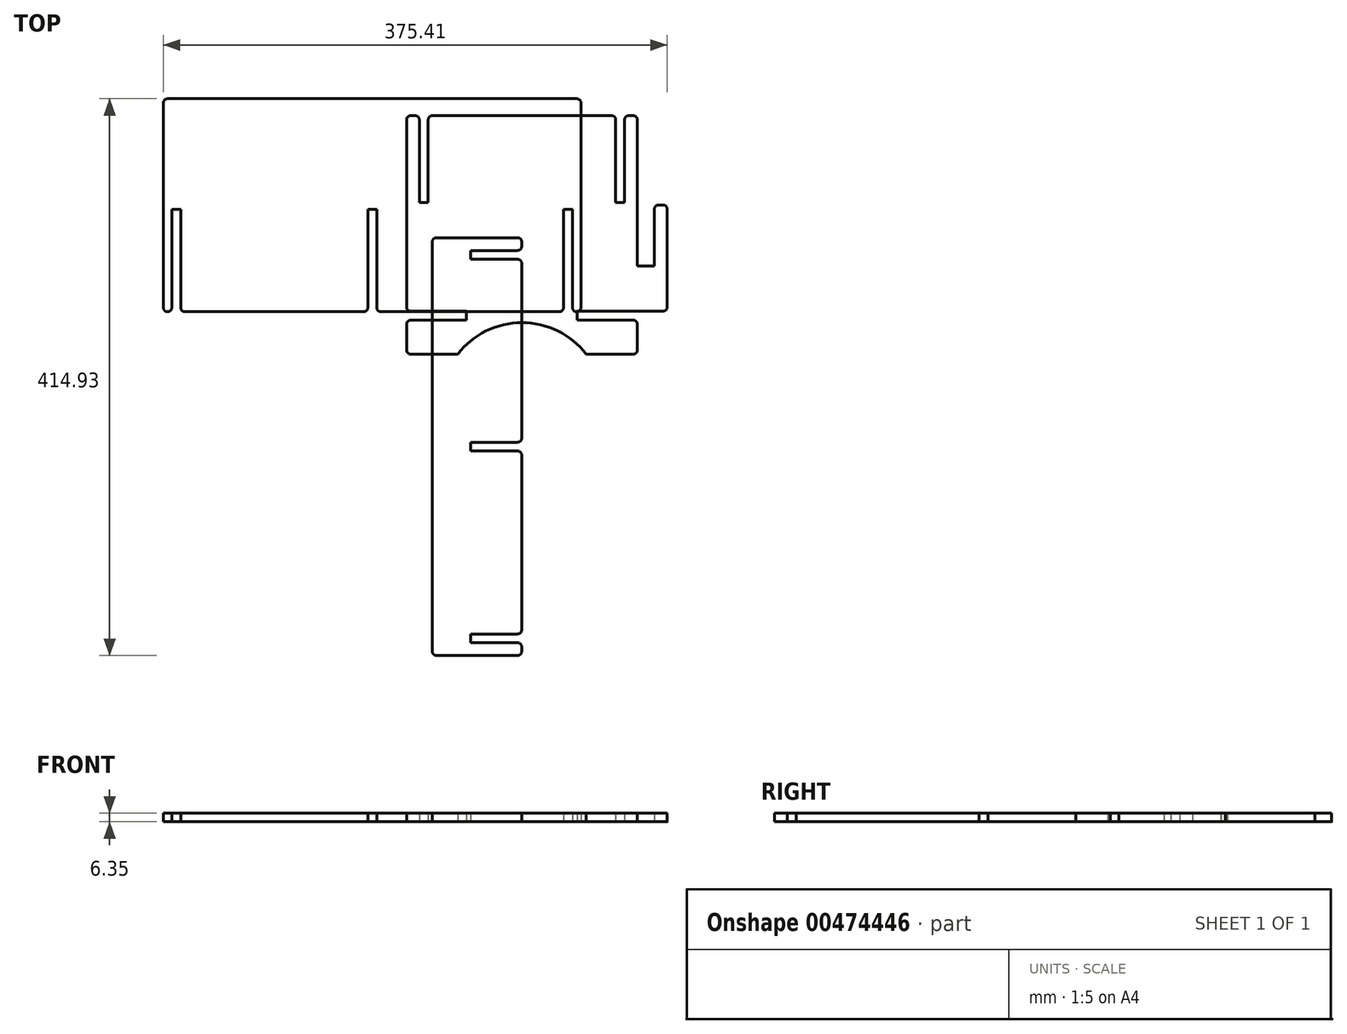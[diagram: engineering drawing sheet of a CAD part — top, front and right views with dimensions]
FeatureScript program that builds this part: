
annotation { "Feature Type Name" : "Feature", "Feature Type Description" : "" }
export const myFeature = defineFeature(function(context is Context, id is Id, definition is map)
    precondition{}
    {
        {
            var Q0;
            Q0=qCreatedBy(makeId("Top.planeOp"),FACE);
            var sketch = newSketch(context, id + "F0", { "sketchPlane" : qUnion([Q0])});
            skLineSegment(sketch, "E0", {"start": v(0, 9.78) * mm, "end": v(0, 149.22) * mm});
            skLineSegment(sketch, "E1", {"start": v(3.17, 152.4) * mm, "end": v(6.35, 152.4) * mm});
            skLineSegment(sketch, "E2", {"start": v(3.17, 0) * mm, "end": v(44.45, 0) * mm});
            skLineSegment(sketch, "E3", {"start": v(171.96, 149.22) * mm, "end": v(171.96, 40.3) * mm});
            skLineSegment(sketch, "E4", {"start": v(168.78, -25.4) * mm, "end": v(133.86, -25.4) * mm});
            skLineSegment(sketch, "E5", {"start": v(0, -3.18) * mm, "end": v(0, -22.22) * mm});
            skLineSegment(sketch, "E6", {"start": v(3.18, -25.4) * mm, "end": v(38.1, -25.4) * mm});
            skLineSegment(sketch, "E7", {"start": v(171.96, -22.23) * mm, "end": v(171.96, -3.18) * mm});
            skLineSegment(sketch, "E8", {"start": v(3.17, 6.6) * mm, "end": v(44.45, 6.6) * mm});
            skLineSegment(sketch, "E9", {"start": v(44.45, 6.6) * mm, "end": v(44.45, 0) * mm});
            skLineSegment(sketch, "E10", {"start": v(171.96, 6.6) * mm, "end": v(127, 6.6) * mm});
            skLineSegment(sketch, "E11", {"start": v(127, 6.6) * mm, "end": v(127, 0) * mm});
            skLineSegment(sketch, "E12", {"start": v(9.53, 149.22) * mm, "end": v(9.53, 87.56) * mm});
            skLineSegment(sketch, "E13", {"start": v(9.53, 87.56) * mm, "end": v(16.13, 87.56) * mm});
            skLineSegment(sketch, "E14", {"start": v(16.13, 87.56) * mm, "end": v(16.13, 149.22) * mm});
            skLineSegment(sketch, "E15.trimOffspring", {"start": v(19.3, 152.4) * mm, "end": v(152.65, 152.4) * mm});
            skLineSegment(sketch, "E16", {"start": v(162.43, 149.22) * mm, "end": v(162.43, 87.56) * mm});
            skLineSegment(sketch, "E17", {"start": v(162.43, 87.56) * mm, "end": v(155.83, 87.56) * mm});
            skLineSegment(sketch, "E18", {"start": v(155.83, 87.56) * mm, "end": v(155.83, 149.22) * mm});
            skLineSegment(sketch, "E19.trimOffspring", {"start": v(165.6, 152.4) * mm, "end": v(168.78, 152.4) * mm});
            skLineSegment(sketch, "E20", {"start": v(171.96, 6.6) * mm, "end": v(191, 6.6) * mm});
            skLineSegment(sketch, "E21", {"start": v(194.18, 9.78) * mm, "end": v(194.18, 82.7) * mm});
            skLineSegment(sketch, "E22", {"start": v(184.66, 40.3) * mm, "end": v(171.96, 40.3) * mm});
            skLineSegment(sketch, "E23", {"start": v(184.66, 40.3) * mm, "end": v(184.66, 82.7) * mm});
            skLineSegment(sketch, "E24", {"start": v(187.83, 85.87) * mm, "end": v(191, 85.87) * mm});
            skPoint(sketch, "E25.end.orphan", {"position": v(85.98, 0) * mm});
            skLineSegment(sketch, "E26.trimOffspring", {"start": v(127, 0) * mm, "end": v(168.78, 0) * mm});
            skArc(sketch, "E27", {"start": v(133.86, -25.4) * mm, "mid": v(85.98, -1.86) * mm, "end": v(38.1, -25.4) * mm});
            skPoint(sketch, "E28.visualSharp", {"position": v(0, 152.4) * mm});
            skArc(sketch, "E28.filletArc", {"start": v(3.18, 152.4) * mm, "mid": v(0.93, 151.47) * mm, "end": v(0, 149.22) * mm});
            skPoint(sketch, "E29.visualSharp", {"position": v(9.53, 152.4) * mm});
            skArc(sketch, "E29.filletArc", {"start": v(9.53, 149.22) * mm, "mid": v(8.6, 151.47) * mm, "end": v(6.35, 152.4) * mm});
            skPoint(sketch, "E30.visualSharp", {"position": v(16.13, 152.4) * mm});
            skArc(sketch, "E30.filletArc", {"start": v(19.3, 152.4) * mm, "mid": v(17.06, 151.47) * mm, "end": v(16.13, 149.22) * mm});
            skPoint(sketch, "E31.visualSharp", {"position": v(155.83, 152.4) * mm});
            skArc(sketch, "E31.filletArc", {"start": v(155.83, 149.22) * mm, "mid": v(154.9, 151.47) * mm, "end": v(152.65, 152.4) * mm});
            skPoint(sketch, "E32.visualSharp", {"position": v(162.43, 152.4) * mm});
            skArc(sketch, "E32.filletArc", {"start": v(165.6, 152.4) * mm, "mid": v(163.36, 151.47) * mm, "end": v(162.43, 149.22) * mm});
            skPoint(sketch, "E33.visualSharp", {"position": v(171.96, 152.4) * mm});
            skArc(sketch, "E33.filletArc", {"start": v(171.96, 149.22) * mm, "mid": v(171.03, 151.47) * mm, "end": v(168.78, 152.4) * mm});
            skPoint(sketch, "E34.visualSharp", {"position": v(184.66, 85.87) * mm});
            skArc(sketch, "E34.filletArc", {"start": v(187.83, 85.87) * mm, "mid": v(185.59, 84.94) * mm, "end": v(184.66, 82.7) * mm});
            skPoint(sketch, "E35.visualSharp", {"position": v(194.18, 85.87) * mm});
            skArc(sketch, "E35.filletArc", {"start": v(194.18, 82.7) * mm, "mid": v(193.25, 84.94) * mm, "end": v(191, 85.87) * mm});
            skPoint(sketch, "E36.visualSharp", {"position": v(0, 6.6) * mm});
            skArc(sketch, "E36.filletArc", {"start": v(0, 9.78) * mm, "mid": v(0.93, 7.53) * mm, "end": v(3.17, 6.6) * mm});
            skPoint(sketch, "E37.visualSharp", {"position": v(0, 0) * mm});
            skArc(sketch, "E37.filletArc", {"start": v(3.17, 0) * mm, "mid": v(0.93, -0.93) * mm, "end": v(0, -3.18) * mm});
            skPoint(sketch, "E38.visualSharp", {"position": v(0, -25.4) * mm});
            skArc(sketch, "E38.filletArc", {"start": v(0, -22.22) * mm, "mid": v(0.93, -24.47) * mm, "end": v(3.18, -25.4) * mm});
            skPoint(sketch, "E39.visualSharp", {"position": v(171.96, -25.4) * mm});
            skArc(sketch, "E39.filletArc", {"start": v(168.78, -25.4) * mm, "mid": v(171.03, -24.47) * mm, "end": v(171.96, -22.23) * mm});
            skPoint(sketch, "E40.visualSharp", {"position": v(171.96, 0) * mm});
            skArc(sketch, "E40.filletArc", {"start": v(171.96, -3.18) * mm, "mid": v(171.03, -0.93) * mm, "end": v(168.78, 0) * mm});
            skPoint(sketch, "E41.visualSharp", {"position": v(194.18, 6.6) * mm});
            skArc(sketch, "E41.filletArc", {"start": v(191, 6.6) * mm, "mid": v(193.25, 7.53) * mm, "end": v(194.18, 9.78) * mm});
            skSolve(sketch);
        }
        {
            var Q0;
            Q0=qCreatedBy(makeId("Top.planeOp"),FACE);
            var sketch = newSketch(context, id + "F1", { "sketchPlane" : qUnion([Q0])});
            skLineSegment(sketch, "E42.bottom", {"start": v(22.32, 61.44) * mm, "end": v(82.65, 61.44) * mm});
            skLineSegment(sketch, "E42.top", {"start": v(22.32, -249.96) * mm, "end": v(82.65, -249.96) * mm});
            skLineSegment(sketch, "E42.left", {"start": v(19.15, 58.27) * mm, "end": v(19.15, -246.79) * mm});
            skLineSegment(sketch, "E42.right", {"start": v(85.82, 58.27) * mm, "end": v(85.82, 55.1) * mm});
            skLineSegment(sketch, "E43.bottom", {"start": v(82.65, 51.92) * mm, "end": v(47.72, 51.92) * mm});
            skLineSegment(sketch, "E43.top", {"start": v(82.65, 45.31) * mm, "end": v(47.72, 45.31) * mm});
            skLineSegment(sketch, "E43.right", {"start": v(47.72, 51.92) * mm, "end": v(47.72, 45.31) * mm});
            skLineSegment(sketch, "E44.bottom", {"start": v(82.65, -90.96) * mm, "end": v(47.72, -90.96) * mm});
            skLineSegment(sketch, "E44.top", {"start": v(82.65, -97.56) * mm, "end": v(47.72, -97.56) * mm});
            skLineSegment(sketch, "E44.right", {"start": v(47.72, -90.96) * mm, "end": v(47.72, -97.56) * mm});
            skLineSegment(sketch, "E45.bottom", {"start": v(82.65, -233.83) * mm, "end": v(47.72, -233.83) * mm});
            skLineSegment(sketch, "E45.top", {"start": v(82.65, -240.44) * mm, "end": v(47.72, -240.44) * mm});
            skLineSegment(sketch, "E45.right", {"start": v(47.72, -233.83) * mm, "end": v(47.72, -240.44) * mm});
            skLineSegment(sketch, "E46.trimOffspring", {"start": v(85.82, -243.61) * mm, "end": v(85.82, -246.79) * mm});
            skLineSegment(sketch, "E47.trimOffspring", {"start": v(85.82, -100.74) * mm, "end": v(85.82, -230.66) * mm});
            skLineSegment(sketch, "E48.trimOffspring", {"start": v(85.82, 42.14) * mm, "end": v(85.82, -87.78) * mm});
            skPoint(sketch, "E49.visualSharp", {"position": v(19.15, 61.44) * mm});
            skArc(sketch, "E49.filletArc", {"start": v(22.32, 61.44) * mm, "mid": v(20.08, 60.51) * mm, "end": v(19.15, 58.27) * mm});
            skPoint(sketch, "E50.visualSharp", {"position": v(85.82, 61.44) * mm});
            skArc(sketch, "E50.filletArc", {"start": v(85.82, 58.27) * mm, "mid": v(84.9, 60.51) * mm, "end": v(82.65, 61.44) * mm});
            skPoint(sketch, "E51.visualSharp", {"position": v(85.82, 51.92) * mm});
            skArc(sketch, "E51.filletArc", {"start": v(82.65, 51.92) * mm, "mid": v(84.9, 52.85) * mm, "end": v(85.82, 55.1) * mm});
            skPoint(sketch, "E52.visualSharp", {"position": v(85.82, 45.31) * mm});
            skArc(sketch, "E52.filletArc", {"start": v(85.82, 42.14) * mm, "mid": v(84.9, 44.38) * mm, "end": v(82.65, 45.31) * mm});
            skPoint(sketch, "E53.visualSharp", {"position": v(85.82, -97.56) * mm});
            skArc(sketch, "E53.filletArc", {"start": v(85.82, -100.74) * mm, "mid": v(84.9, -98.5) * mm, "end": v(82.65, -97.56) * mm});
            skPoint(sketch, "E54.visualSharp", {"position": v(85.82, -90.96) * mm});
            skArc(sketch, "E54.filletArc", {"start": v(82.65, -90.96) * mm, "mid": v(84.9, -90.03) * mm, "end": v(85.82, -87.78) * mm});
            skPoint(sketch, "E55.visualSharp", {"position": v(85.82, -233.83) * mm});
            skArc(sketch, "E55.filletArc", {"start": v(82.65, -233.83) * mm, "mid": v(84.9, -232.9) * mm, "end": v(85.82, -230.66) * mm});
            skPoint(sketch, "E56.visualSharp", {"position": v(85.82, -240.44) * mm});
            skArc(sketch, "E56.filletArc", {"start": v(85.82, -243.61) * mm, "mid": v(84.9, -241.37) * mm, "end": v(82.65, -240.44) * mm});
            skPoint(sketch, "E57.visualSharp", {"position": v(85.82, -249.96) * mm});
            skArc(sketch, "E57.filletArc", {"start": v(82.65, -249.96) * mm, "mid": v(84.9, -249.03) * mm, "end": v(85.82, -246.79) * mm});
            skPoint(sketch, "E58.visualSharp", {"position": v(19.15, -249.96) * mm});
            skArc(sketch, "E58.filletArc", {"start": v(19.15, -246.79) * mm, "mid": v(20.08, -249.03) * mm, "end": v(22.32, -249.96) * mm});
            skSolve(sketch);
        }
        {
            var Q0;
            Q0=qCreatedBy(makeId("Top.planeOp"),FACE);
            var sketch = newSketch(context, id + "F2", { "sketchPlane" : qUnion([Q0])});
            skLineSegment(sketch, "E59.bottom", {"start": v(126.75, 164.97) * mm, "end": v(-178.05, 164.97) * mm});
            skLineSegment(sketch, "E59.top", {"start": v(126.75, 6.22) * mm, "end": v(126.75, 6.22) * mm});
            skLineSegment(sketch, "E59.left", {"start": v(129.92, 161.8) * mm, "end": v(129.92, 9.4) * mm});
            skLineSegment(sketch, "E59.right", {"start": v(-181.23, 161.8) * mm, "end": v(-181.23, 9.4) * mm});
            skLineSegment(sketch, "E60.bottom", {"start": v(-22.21, 82.58) * mm, "end": v(-28.81, 82.42) * mm});
            skLineSegment(sketch, "E60.left", {"start": v(-22.21, 82.58) * mm, "end": v(-22.21, 9.4) * mm});
            skLineSegment(sketch, "E60.right", {"start": v(-28.81, 82.42) * mm, "end": v(-28.81, 9.4) * mm});
            skLineSegment(sketch, "E61.top", {"start": v(-174.88, 82.42) * mm, "end": v(-168.27, 82.42) * mm});
            skLineSegment(sketch, "E61.left", {"start": v(-174.88, 9.4) * mm, "end": v(-174.88, 82.42) * mm});
            skLineSegment(sketch, "E61.right", {"start": v(-168.27, 9.4) * mm, "end": v(-168.27, 82.42) * mm});
            skLineSegment(sketch, "E62.top", {"start": v(123.57, 82.42) * mm, "end": v(116.97, 82.42) * mm});
            skLineSegment(sketch, "E62.left", {"start": v(123.57, 9.4) * mm, "end": v(123.57, 82.42) * mm});
            skLineSegment(sketch, "E62.right", {"start": v(116.97, 9.4) * mm, "end": v(116.97, 82.42) * mm});
            skLineSegment(sketch, "E63.trimOffspring", {"start": v(-178.05, 6.22) * mm, "end": v(-178.05, 6.22) * mm});
            skLineSegment(sketch, "E64.trimOffspring", {"start": v(-31.99, 6.22) * mm, "end": v(-165.1, 6.22) * mm});
            skLineSegment(sketch, "E65.trimOffspring", {"start": v(113.8, 6.22) * mm, "end": v(-19.04, 6.22) * mm});
            skPoint(sketch, "E66.visualSharp", {"position": v(-181.23, 164.97) * mm});
            skArc(sketch, "E66.filletArc", {"start": v(-178.05, 164.97) * mm, "mid": v(-180.3, 164.04) * mm, "end": v(-181.23, 161.8) * mm});
            skPoint(sketch, "E67.visualSharp", {"position": v(-181.23, 6.22) * mm});
            skArc(sketch, "E67.filletArc", {"start": v(-181.23, 9.4) * mm, "mid": v(-180.3, 7.15) * mm, "end": v(-178.05, 6.22) * mm});
            skPoint(sketch, "E68.visualSharp", {"position": v(-168.27, 6.22) * mm});
            skArc(sketch, "E68.filletArc", {"start": v(-168.27, 9.4) * mm, "mid": v(-167.34, 7.15) * mm, "end": v(-165.1, 6.22) * mm});
            skPoint(sketch, "E69.visualSharp", {"position": v(-28.81, 6.22) * mm});
            skArc(sketch, "E69.filletArc", {"start": v(-31.99, 6.22) * mm, "mid": v(-29.74, 7.15) * mm, "end": v(-28.81, 9.4) * mm});
            skPoint(sketch, "E70.visualSharp", {"position": v(-22.21, 6.22) * mm});
            skArc(sketch, "E70.filletArc", {"start": v(-22.21, 9.4) * mm, "mid": v(-21.28, 7.15) * mm, "end": v(-19.04, 6.22) * mm});
            skPoint(sketch, "E71.visualSharp", {"position": v(116.97, 6.22) * mm});
            skArc(sketch, "E71.filletArc", {"start": v(113.8, 6.22) * mm, "mid": v(116.04, 7.15) * mm, "end": v(116.97, 9.4) * mm});
            skPoint(sketch, "E72.visualSharp", {"position": v(129.92, 6.22) * mm});
            skArc(sketch, "E72.filletArc", {"start": v(126.75, 6.22) * mm, "mid": v(129, 7.15) * mm, "end": v(129.92, 9.4) * mm});
            skPoint(sketch, "E73.visualSharp", {"position": v(123.57, 6.22) * mm});
            skArc(sketch, "E73.filletArc", {"start": v(123.57, 9.4) * mm, "mid": v(124.5, 7.15) * mm, "end": v(126.75, 6.22) * mm});
            skPoint(sketch, "E74.visualSharp", {"position": v(-174.88, 6.22) * mm});
            skArc(sketch, "E74.filletArc", {"start": v(-178.05, 6.22) * mm, "mid": v(-175.8, 7.15) * mm, "end": v(-174.88, 9.4) * mm});
            skPoint(sketch, "E75.visualSharp", {"position": v(129.92, 164.97) * mm});
            skArc(sketch, "E75.filletArc", {"start": v(129.92, 161.8) * mm, "mid": v(129, 164.04) * mm, "end": v(126.75, 164.97) * mm});
            skSolve(sketch);
        }
        {
            var Q0;
            Q0 = qSketchRegion(id + "F1", true);
            extrude(context, id + "F3", {"entities" : qUnion([Q0]), "depth" : 6.35 * mm, "offsetDistance" : 25.4 * mm});
        }
        {
            var Q0;
            Q0 = qSketchRegion(id + "F1", true);
            extrude(context, id + "F4", {"entities" : qUnion([Q0]), "operationType" : NewBodyOperationType.ADD, "depth" : 6.35 * mm});
        }
        {
            var Q0;
            Q0 = qSketchRegion(id + "F2", true);
            extrude(context, id + "F5", {"entities" : qUnion([Q0]), "depth" : 6.35 * mm, "offsetDistance" : 25.4 * mm});
        }
        {
            var Q0;
            Q0=makeQuery(id+"F0.imprint","IMPRINT",FACE,{"disambiguationData":[TD([[makeQuery(id+"F0.imprint","IMPRINT",EDGE,{"derivedFrom":sQuery(id+"F0.wireOp",EDGE,"E0")}),-1.0]])]});
            extrude(context, id + "F6", {"entities" : qUnion([Q0]), "depth" : 6.35 * mm, "offsetDistance" : 25.4 * mm});
        }
    });
